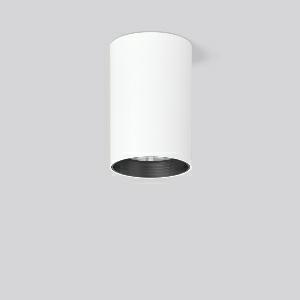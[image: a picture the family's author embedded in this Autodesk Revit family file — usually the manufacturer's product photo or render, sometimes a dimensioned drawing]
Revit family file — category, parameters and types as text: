
# Revit family: heledon_maxi_a_931220_002_1_76_35ff
name_source: partatom
category: Lighting Fixtures
units: mm (PartAtom-declared; Revit-internal decimal feet)

## family parameters
Cut with Voids When Loaded = No
Host = Face
Light Source = No
Part Type = Normal
Room Calculation Point = No
Round Connector Dimension = Use Diameter
Shared = No

## types (1)
- HELEDON maxi A (1 x LED Modul 940, 3000 lm, 4000)
    Apparent Load = 25 VA
    Approval mark = CE
    CIE Flux Codes = 97 100 100 100 100
    Color Rendering = 92
    Color Temperature = 4000
    Default Elevation = 1800 mm
    Description = Series: HELEDON maxi
Cylindrical surface-mounted downlight. Housing: die-cast aluminium, powder-coated. Internal ceiling frame polycarbonate with bayonet mounting. Black plastic ring and recessed LED to prevent glare from the side. Optical assembly with lens made of plastic (polycarbonate) for the best homogeneous light distribution - can be changed without tools. Best colour rendering index Ra>90. Suitable for Ceiling mounting. Easy installation with a separate ceiling frame with bayonet mounting and plug connection. Driver integrated. Connected via plug-in connector. High quality converter without flickering and stroboscopic effect. The following accessories can be mounted without use of tools: interchangeable lenses, decorative glasses, honeycomb louvre, clear and frosted diffusers, white interchangeable plastic ring. 
Colour: traffic white, matt (RAL 9016)
Diameter: 123 mm
Height: 183 mm
Lamp: LED
Socket: without socket
Colour temperature: 4000K
Colour rendering index (CRI): 92
System power: 25 W
Rated luminous flux: 3000 lm
Luminous efficiency: 120 lm/W
Control gear: Converter, dimmable, DALI
Protection class: I
Type of protection: IP 20
    Height = 183 mm
    Lamp = 1 x LED Modul 940
    Lamp Light Flux = 3000 lm
    Lamp count = 1
    Length = 123 mm
    Lifetime = 50000 h
    Luminous efficacy = 120 lm/W
    Manufacturer = RZB
    ModVariant = No
    Model = 931220.002.1.76
    Mounting Place = Ceiling
    Mounting Type = Surface mounted
    Number of Poles = 1
    OnlyDefault = Yes
    Power Factor = 1
    Product Name = HELEDON maxi A
    Product group = Surface mounted downlights
    ProductGroupID = 302
    Protection Class = Protection class I
    Protection Degree = IP 20
    RLX_Detail_Level = 1
    RLX_Emergency_Light_Flux = 0 lm
    RLX_Emergency_Type = 0
    RLX_Emergency_Type_DB = No
    RlxData = <blob elided: 97745 chars, md5=64a35075>
    Socket = socket
    Standby Power = 0 W
    System Light Flux = 3000 lm
    System Power = 25 W
    Type Comments = Product without accessories
    Type Image = 931193.002.jpg
    URL = http://relux.com
    VarID = ---
    Voltage = 230 V
    Voltage Range = 220-240 V
    Weight = 0.00 kg
    Width = 0 mm  [stored 0 ft]

note: [stored X ft] marks values corroborated as IEEE doubles in the binary element streams (Revit-internal decimal feet)

## geometry (parser evidence)
native form markers: Blend x4, Sweep x10
no freeform markers — native parametric forms only
